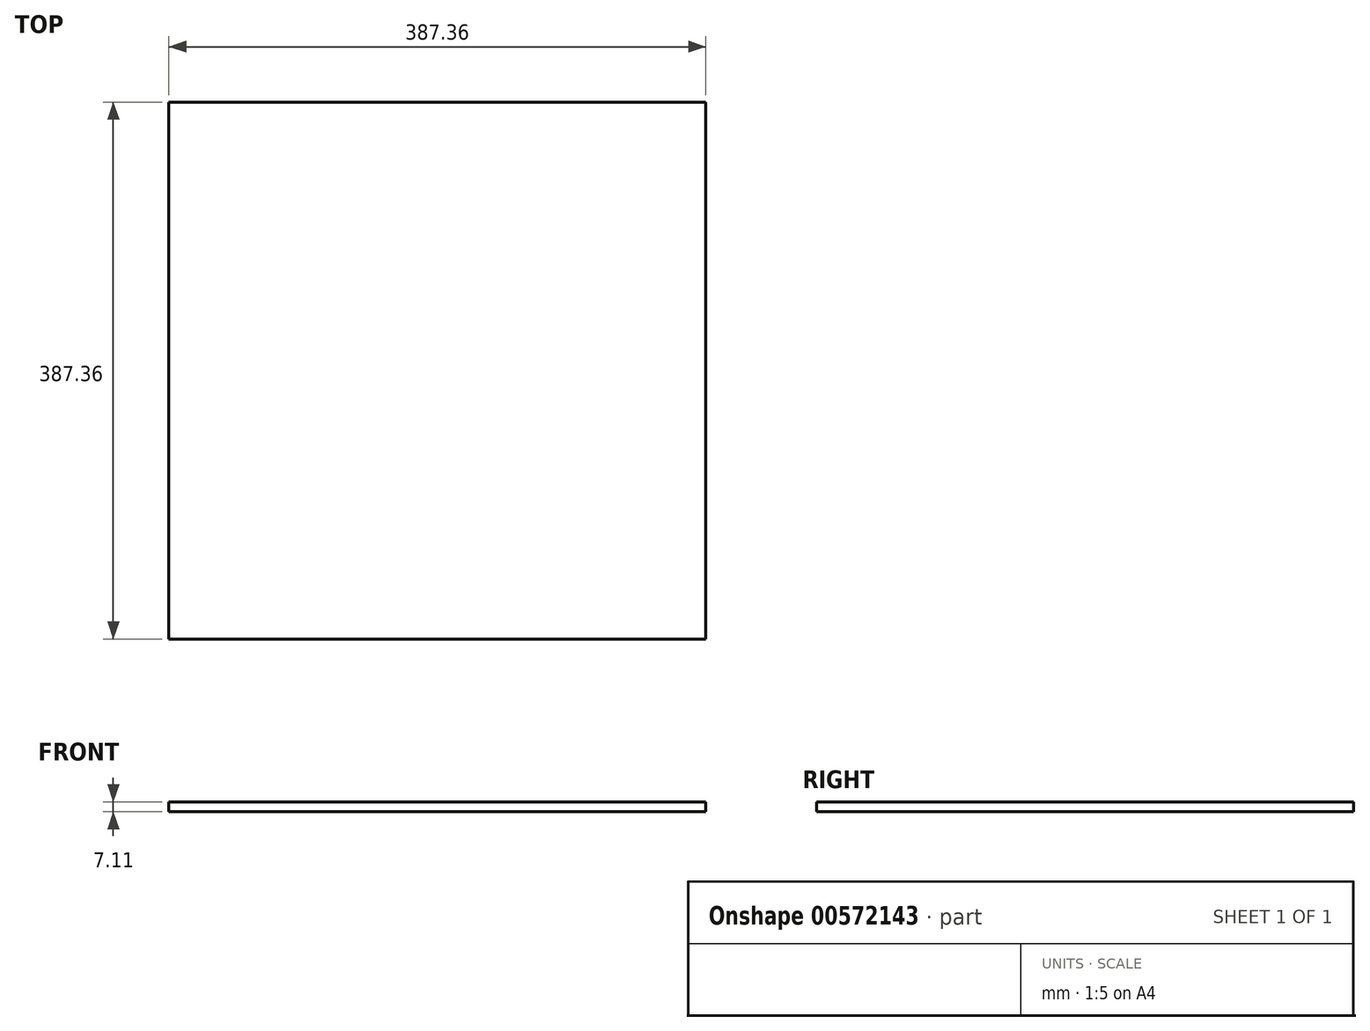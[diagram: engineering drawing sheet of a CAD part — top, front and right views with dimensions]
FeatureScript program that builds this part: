
annotation { "Feature Type Name" : "Feature", "Feature Type Description" : "" }
export const myFeature = defineFeature(function(context is Context, id is Id, definition is map)
    precondition{}
    {
        {
            var Q0;
            Q0=qCreatedBy(makeId("Top.planeOp"),FACE);
            var sketch = newSketch(context, id + "F0", { "sketchPlane" : qUnion([Q0])});
            skLineSegment(sketch, "E0.bottom", {"start": v(193.67, 193.68) * mm, "end": v(-193.68, 193.68) * mm});
            skLineSegment(sketch, "E0.top", {"start": v(193.68, -193.68) * mm, "end": v(-193.68, -193.68) * mm});
            skLineSegment(sketch, "E0.left", {"start": v(193.67, 193.68) * mm, "end": v(193.68, -193.68) * mm});
            skLineSegment(sketch, "E0.right", {"start": v(-193.68, 193.68) * mm, "end": v(-193.68, -193.68) * mm});
            skPoint(sketch, "E0.middle", {"position": v(0, 0) * mm});
            skSolve(sketch);
        }
        {
            var Q0;
            Q0=makeQuery(id+"F0.imprint","IMPRINT",FACE,{"disambiguationData":[TD([[makeQuery(id+"F0.imprint","IMPRINT",EDGE,{"derivedFrom":sQuery(id+"F0.wireOp",EDGE,"E0.bottom")}),1.0]])]});
            extrude(context, id + "F1", {"entities" : qUnion([Q0]), "depth" : 7.11 * mm, "offsetDistance" : 25.4 * mm});
        }
    });
